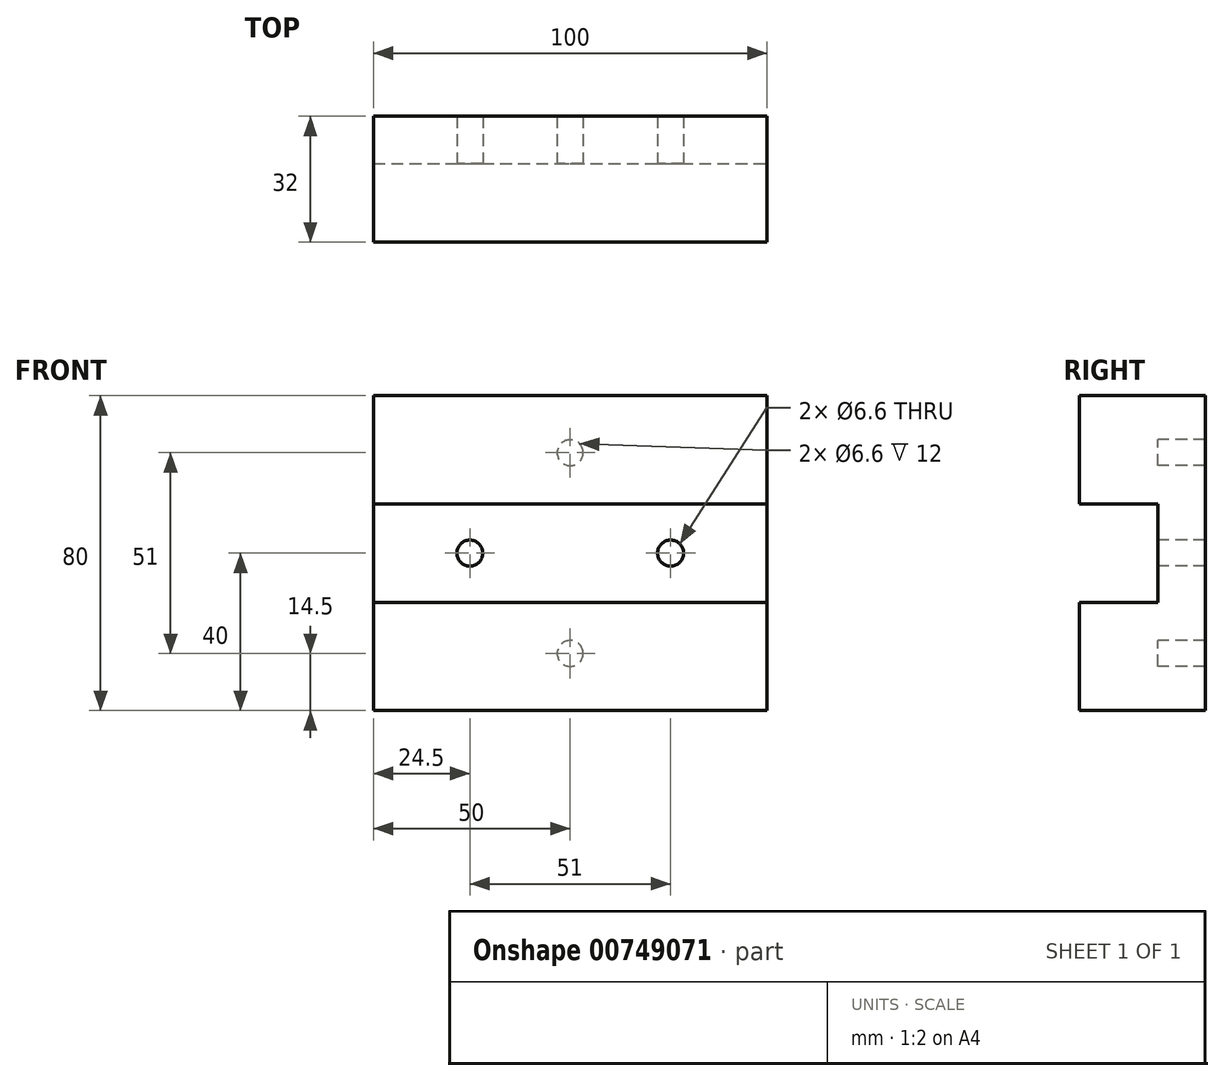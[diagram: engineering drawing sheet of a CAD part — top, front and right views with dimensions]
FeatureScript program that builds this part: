
annotation { "Feature Type Name" : "Feature", "Feature Type Description" : "" }
export const myFeature = defineFeature(function(context is Context, id is Id, definition is map)
    precondition{}
    {
        {
            var Q0;
            Q0=qCreatedBy(makeId("Front.planeOp"),FACE);
            var sketch = newSketch(context, id + "F0", { "sketchPlane" : qUnion([Q0])});
            skLineSegment(sketch, "E0.bottom", {"start": v(0, 0) * mm, "end": v(-100, 0) * mm});
            skLineSegment(sketch, "E0.top", {"start": v(0, 80) * mm, "end": v(-100, 80) * mm});
            skLineSegment(sketch, "E0.left", {"start": v(0, 0) * mm, "end": v(0, 80) * mm});
            skLineSegment(sketch, "E0.right", {"start": v(-100, 0) * mm, "end": v(-100, 80) * mm});
            skLineSegment(sketch, "E1", {"start": v(-100, 40) * mm, "end": v(0, 40) * mm, "construction": true});
            skLineSegment(sketch, "E2", {"start": v(-50, 0) * mm, "end": v(-50, 80) * mm, "construction": true});
            skPoint(sketch, "E3", {"position": v(-50, 65.5) * mm});
            skPoint(sketch, "E4.MirrorP", {"position": v(-50, 14.5) * mm});
            skPoint(sketch, "E5", {"position": v(-75.5, 40) * mm});
            skPoint(sketch, "E6.MirrorP", {"position": v(-24.5, 40) * mm});
            skSolve(sketch);
        }
        {
            var Q0;
            Q0 = qSketchRegion(id + "F0", true);
            extrude(context, id + "F1", {"entities" : qUnion([Q0]), "depth" : 12 * mm, "offsetDistance" : 25 * mm});
        }
        {
            var Q0;
            Q0=sQuery(id+"F0.wireOp",VERTEX,"E5");
            var Q1;
            Q1=sQuery(id+"F0.wireOp",VERTEX,"E4.MirrorP");
            var Q2;
            Q2=sQuery(id+"F0.wireOp",VERTEX,"E3");
            var Q3;
            Q3=sQuery(id+"F0.wireOp",VERTEX,"E6.MirrorP");
            var Q4;
            Q4=makeQuery(id+"F1.opExtrude","SWEPT_BODY",BODY,{"disambiguationData":[OSD([sQuery(id+"F0.wireOp",EDGE,"E0.bottom"),sQuery(id+"F0.wireOp",EDGE,"E0.top"),sQuery(id+"F0.wireOp",EDGE,"E0.left"),sQuery(id+"F0.wireOp",EDGE,"E0.right")])]});
            hole(context, id + "F2", {"style" : HoleStyle.SIMPLE, "endStyle" : HoleEndStyle.BLIND, "oppositeDirection" : true, "standardTappedOrClearance" : lookupTablePath({ "standard" : "ISO", "fit" : "Normal", "size" : "M6", "type" : "Clearance" }), "standardBlindInLast" : lookupTablePath({ "fit" : "Standard", "standard" : "ISO", "size" : "M6", "type" : "Clearance" }), "holeDiameter" : 6.6 * mm, "majorDiameter" : 5 * mm, "holeDepth" : 12 * mm, "isTappedThrough" : true, "tappedDepth" : 1.9 * mm, "tapClearance" : 3, "locations" : qUnion([Q0, Q1, Q2, Q3]), "scope" : qUnion([Q4])});
        }
        {
            var Q0;
            Q0=makeQuery(id+"F1.opExtrude","CAP_FACE",FACE,{"disambiguationData":[OSD([sQuery(id+"F0.wireOp",EDGE,"E0.bottom"),sQuery(id+"F0.wireOp",EDGE,"E0.top"),sQuery(id+"F0.wireOp",EDGE,"E0.left"),sQuery(id+"F0.wireOp",EDGE,"E0.right")])],"isStart":false});
            var sketch = newSketch(context, id + "F3", { "sketchPlane" : qUnion([Q0])});
            skLineSegment(sketch, "E7.bottom", {"start": v(-100, 0) * mm, "end": v(0, 0) * mm});
            skLineSegment(sketch, "E7.top", {"start": v(-100, 27.5) * mm, "end": v(0, 27.5) * mm});
            skLineSegment(sketch, "E7.left", {"start": v(-100, 0) * mm, "end": v(-100, 27.5) * mm});
            skLineSegment(sketch, "E7.right", {"start": v(0, 0) * mm, "end": v(0, 27.5) * mm});
            skLineSegment(sketch, "E8.0", {"start": v(-100, 40) * mm, "end": v(0, 40) * mm, "construction": true});
            skLineSegment(sketch, "E9.MirrorCS", {"start": v(-100, 52.5) * mm, "end": v(0, 52.5) * mm});
            skLineSegment(sketch, "E10.MirrorCS", {"start": v(-100, 80) * mm, "end": v(-100, 52.5) * mm});
            skLineSegment(sketch, "E11.MirrorCS", {"start": v(-100, 80) * mm, "end": v(0, 80) * mm});
            skLineSegment(sketch, "E12.MirrorCS", {"start": v(0, 80) * mm, "end": v(0, 52.5) * mm});
            skSolve(sketch);
        }
        {
            var Q0;
            Q0 = qSketchRegion(id + "F3", true);
            extrude(context, id + "F4", {"entities" : qUnion([Q0]), "operationType" : NewBodyOperationType.ADD, "depth" : 20 * mm, "offsetDistance" : 25 * mm});
        }
    });
